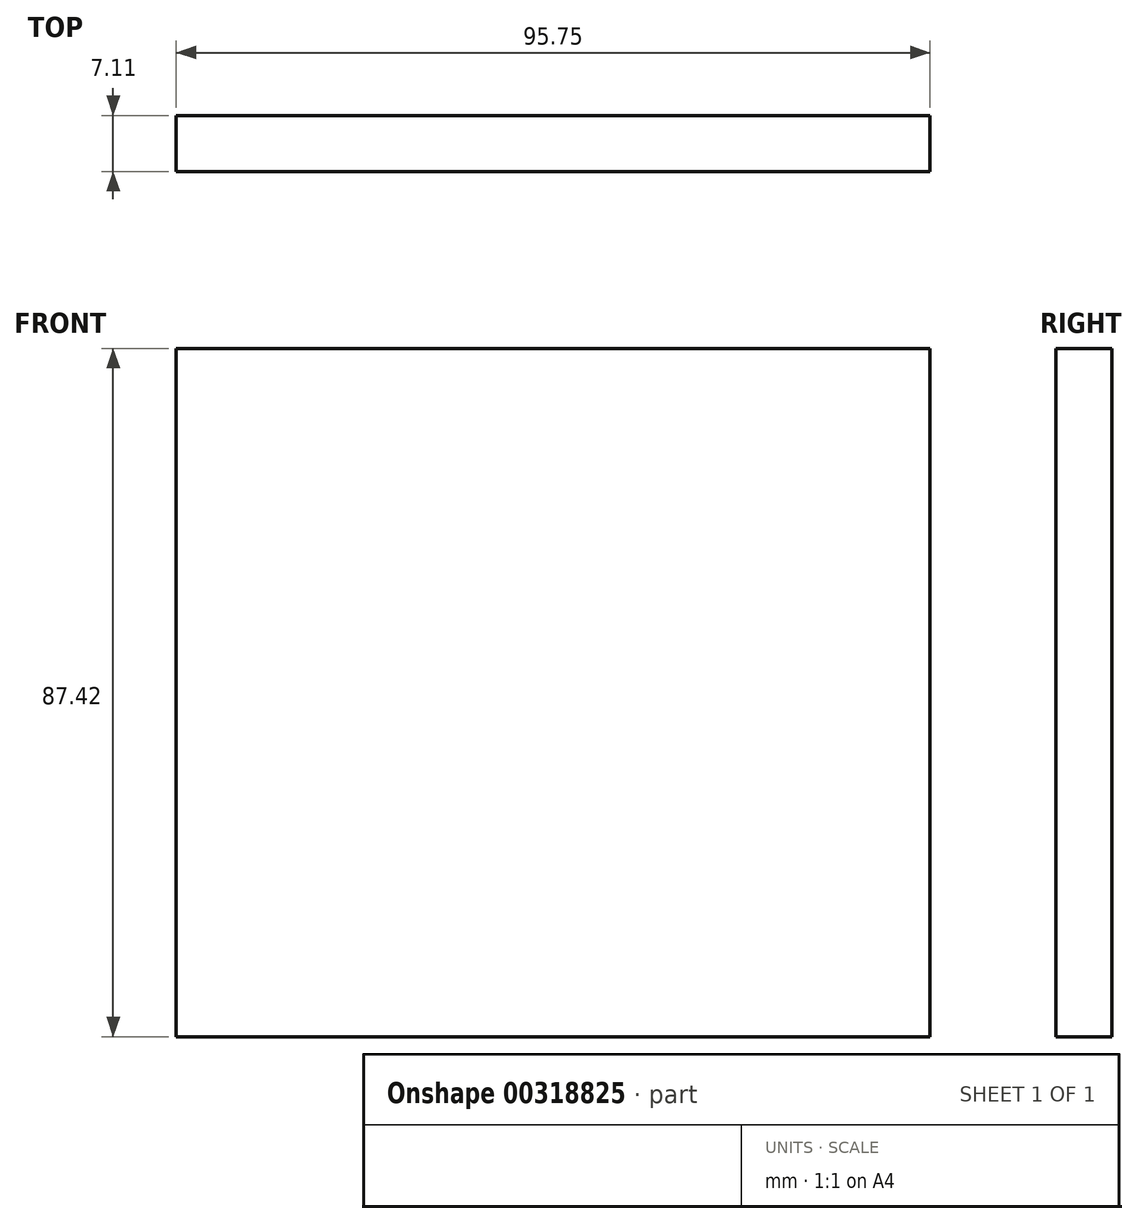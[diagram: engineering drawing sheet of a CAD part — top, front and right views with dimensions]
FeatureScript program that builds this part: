
annotation { "Feature Type Name" : "Feature", "Feature Type Description" : "" }
export const myFeature = defineFeature(function(context is Context, id is Id, definition is map)
    precondition{}
    {
        {
            var Q0;
            Q0=qCreatedBy(makeId("Front.planeOp"),FACE);
            var sketch = newSketch(context, id + "F0", { "sketchPlane" : qUnion([Q0])});
            skLineSegment(sketch, "E0", {"start": v(-55.7, 52.66) * mm, "end": v(-4.93, 52.66) * mm});
            skLineSegment(sketch, "E1.left", {"start": v(-55.7, 52.66) * mm, "end": v(-55.7, 52.66) * mm});
            skLineSegment(sketch, "E1.right", {"start": v(-4.93, 52.66) * mm, "end": v(-4.93, 52.66) * mm});
            skLineSegment(sketch, "E2.bottom", {"start": v(-4.93, -34.76) * mm, "end": v(-55.7, -34.76) * mm});
            skLineSegment(sketch, "E2.top", {"start": v(-4.93, 52.66) * mm, "end": v(-55.7, 52.66) * mm});
            skLineSegment(sketch, "E2.left", {"start": v(-4.93, -34.76) * mm, "end": v(-4.93, 52.66) * mm});
            skLineSegment(sketch, "E2.right", {"start": v(-55.7, -34.76) * mm, "end": v(-55.7, 52.66) * mm});
            skSolve(sketch);
        }
        {
            var Q0;
            Q0=sQuery(id+"F0.wireOp",EDGE,"E2.right");
            extrude(context, id + "F1", {"bodyType" : ToolBodyType.SURFACE, "surfaceEntities" : qUnion([Q0]), "oppositeDirection" : true, "depth" : 7.11 * mm});
        }
        {
            var Q0;
            Q0=makeQuery(id+"F1.opExtrude","SWEPT_FACE",FACE,{"disambiguationData":[OSD([sQuery(id+"F0.wireOp",EDGE,"E2.right")])]});
            extrude(context, id + "F2", {"entities" : qUnion([Q0]), "oppositeDirection" : true, "depth" : 95.76 * mm});
        }
    });
